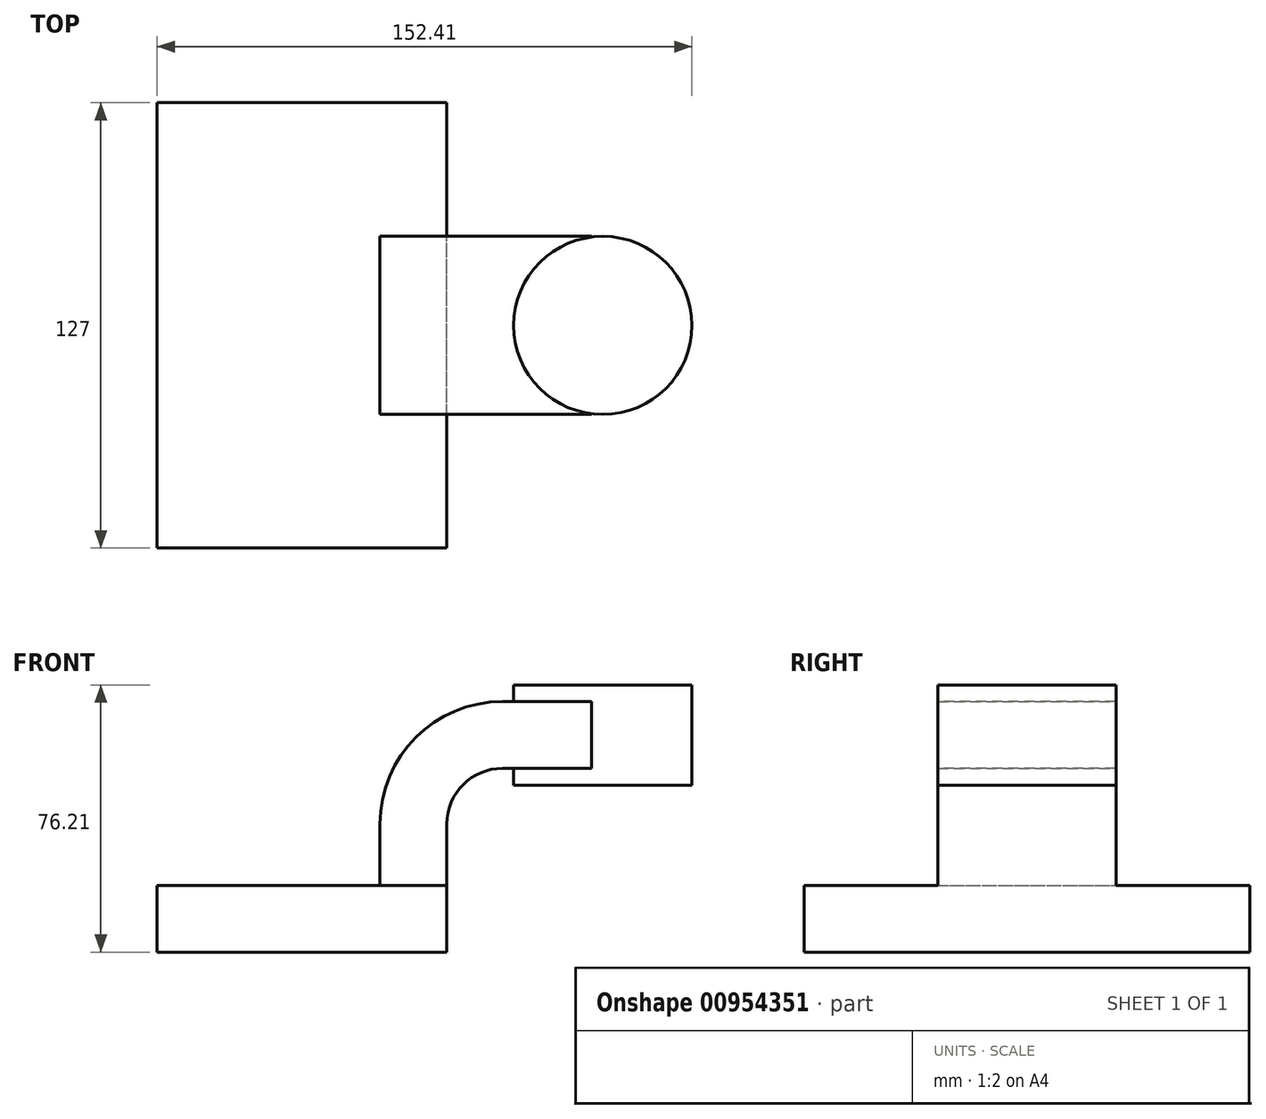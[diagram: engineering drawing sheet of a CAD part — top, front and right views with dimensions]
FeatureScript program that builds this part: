
annotation { "Feature Type Name" : "Feature", "Feature Type Description" : "" }
export const myFeature = defineFeature(function(context is Context, id is Id, definition is map)
    precondition{}
    {
        {
            var Q0;
            Q0=qCreatedBy(makeId("Front.planeOp"),FACE);
            var sketch = newSketch(context, id + "F0", { "sketchPlane" : qUnion([Q0])});
            skLineSegment(sketch, "E0.bottom", {"start": v(41.27, 9.53) * mm, "end": v(-41.28, 9.53) * mm});
            skLineSegment(sketch, "E0.top", {"start": v(41.28, -9.52) * mm, "end": v(-41.27, -9.53) * mm});
            skLineSegment(sketch, "E0.left", {"start": v(41.28, 9.53) * mm, "end": v(41.28, -9.52) * mm});
            skLineSegment(sketch, "E0.right", {"start": v(-41.28, 9.53) * mm, "end": v(-41.27, -9.53) * mm});
            skPoint(sketch, "E0.middle", {"position": v(0, 0) * mm});
            skLineSegment(sketch, "E1.bottom", {"start": v(60.32, 66.68) * mm, "end": v(111.12, 66.68) * mm});
            skLineSegment(sketch, "E1.top", {"start": v(60.32, 38.1) * mm, "end": v(111.12, 38.1) * mm});
            skLineSegment(sketch, "E1.left", {"start": v(60.32, 66.68) * mm, "end": v(60.32, 38.1) * mm});
            skLineSegment(sketch, "E1.right", {"start": v(111.12, 66.68) * mm, "end": v(111.12, 38.1) * mm});
            skPoint(sketch, "E1.middle", {"position": v(85.73, 52.39) * mm});
            skLineSegment(sketch, "E2", {"start": v(41.27, 9.53) * mm, "end": v(41.27, 27) * mm});
            skArc(sketch, "E3", {"start": v(41.27, 27) * mm, "mid": v(45.92, 38.23) * mm, "end": v(57.15, 42.88) * mm});
            skLineSegment(sketch, "E4", {"start": v(57.15, 42.88) * mm, "end": v(82.52, 42.88) * mm});
            skLineSegment(sketch, "E5.0", {"start": v(57.15, 61.93) * mm, "end": v(82.52, 61.93) * mm});
            skArc(sketch, "E5.1", {"start": v(22.23, 27) * mm, "mid": v(32.45, 51.7) * mm, "end": v(57.15, 61.93) * mm});
            skLineSegment(sketch, "E5.2", {"start": v(22.22, 9.53) * mm, "end": v(22.22, 27) * mm});
            skLineSegment(sketch, "E6", {"start": v(82.52, 42.88) * mm, "end": v(82.52, 61.93) * mm});
            skFitSpline(sketch, "E7", {"points": [v(-41.28, 9.52) * mm, v(57.15, 61.93) * mm], "startDerivative": vector(0.16, 66.3) * mm, "endDerivative": vector(88.69, -0.2) * mm});
            skLineSegment(sketch, "E8", {"start": v(85.72, 66.68) * mm, "end": v(85.72, 38.1) * mm});
            skSolve(sketch);
        }
        {
            var Q0;
            Q0=makeQuery(id+"F0.imprint","IMPRINT",FACE,{"disambiguationData":[TD([[makeQuery(id+"F0.imprint","IMPRINT",EDGE,{"derivedFrom":sQuery(id+"F0.wireOp",EDGE,"E0.top")}),-1.0]])]});
            extrude(context, id + "F1", {"entities" : qUnion([Q0]), "endBound" : BoundingType.SYMMETRIC, "depth" : 127 * mm, "offsetDistance" : 25.4 * mm});
        }
        {
            var Q0;
            {var subQ1=sQuery(id+"F0.wireOp",EDGE,"E2");Q0=makeQuery(id+"F0.imprint","IMPRINT",FACE,{"disambiguationData":[TD([[makeQuery(id+"F0.imprint","IMPRINT",EDGE,{"derivedFrom":subQ1}),1.0]])]});}
            var Q1;
            {var subQ5=sQuery(id+"F0.wireOp",EDGE,"E6");Q1=makeQuery(id+"F0.imprint","IMPRINT",FACE,{"disambiguationData":[TD([[makeQuery(id+"F0.imprint","IMPRINT",EDGE,{"derivedFrom":subQ5}),1.0]])]});}
            extrude(context, id + "F2", {"entities" : qUnion([Q0, Q1]), "operationType" : NewBodyOperationType.ADD, "endBound" : BoundingType.SYMMETRIC, "depth" : 50.8 * mm, "offsetDistance" : 25.4 * mm});
        }
        {
            var Q0;
            Q0=makeQuery(id+"F0.imprint","IMPRINT",FACE,{"disambiguationData":[TD([[makeQuery(id+"F0.imprint","IMPRINT",EDGE,{"derivedFrom":sQuery(id+"F0.wireOp",EDGE,"E5.1")}),1.0]])]});
            extrude(context, id + "F3", {"entities" : qUnion([Q0]), "operationType" : NewBodyOperationType.ADD, "endBound" : BoundingType.SYMMETRIC, "depth" : 15.88 * mm, "offsetDistance" : 25.4 * mm});
        }
        {
            var Q0;
            {var subQ0=sQuery(id+"F0.wireOp",EDGE,"E1.right");Q0=makeQuery(id+"F0.imprint","IMPRINT",FACE,{"disambiguationData":[TD([[makeQuery(id+"F0.imprint","IMPRINT",EDGE,{"derivedFrom":subQ0}),-1.0]])]});}
            var Q1;
            Q1=sQuery(id+"F0.wireOp",EDGE,"E8");
            revolve(context, id + "F4", {"operationType" : NewBodyOperationType.ADD, "surfaceOperationType" : NewSurfaceOperationType.NEW, "entities" : qUnion([Q0]), "axis" : qUnion([Q1]), "revolveType" : RevolveType.FULL});
        }
    });
